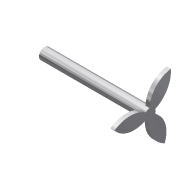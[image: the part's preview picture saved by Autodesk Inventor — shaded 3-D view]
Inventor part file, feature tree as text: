
AUTODESK INVENTOR PART (.ipt)
format: ipt  version: 2015 (Build 190159000, 159)  size: 96,256 bytes
history: native  units: in
note: dims shown in document units (in); Inventor stores cm internally (conversion verified against a paired STEP export)
features: extrude x3, sketch x3, pattern_circular x1
ambient origin geometry x8: Origin, YZ Plane, XZ Plane, XY Plane, X Axis, Y Axis, Z Axis, Center Point
bodies: Solid1 (feature_tree)
feature tree (7):
  extrude  "Extrusion1"  Depth=5.0in TaperAngle=0.0deg
  extrude  "Extrusion2"  Depth=0.1875in TaperAngle=0.0deg
  extrude  "Extrusion3"  [1 undecoded]
  pattern_circular  "Circular Pattern1"  [2 undecoded]
  sketch  "Sketch1"  dims[d0=0.5in d1=5.0in d2=0.0in]
  sketch  "Sketch2"  dims[d3=0.25in d4=0.0in d5=0.1875in d6=0.0in]
  sketch  "Sketch3"  dims[d7=1.1811in d8=360.0deg]
note: 3 required parameter values undecoded (feature->parameter linkage not recoverable at this tier; creation-order binding heuristic only, values carry confidence <= 0.55)
